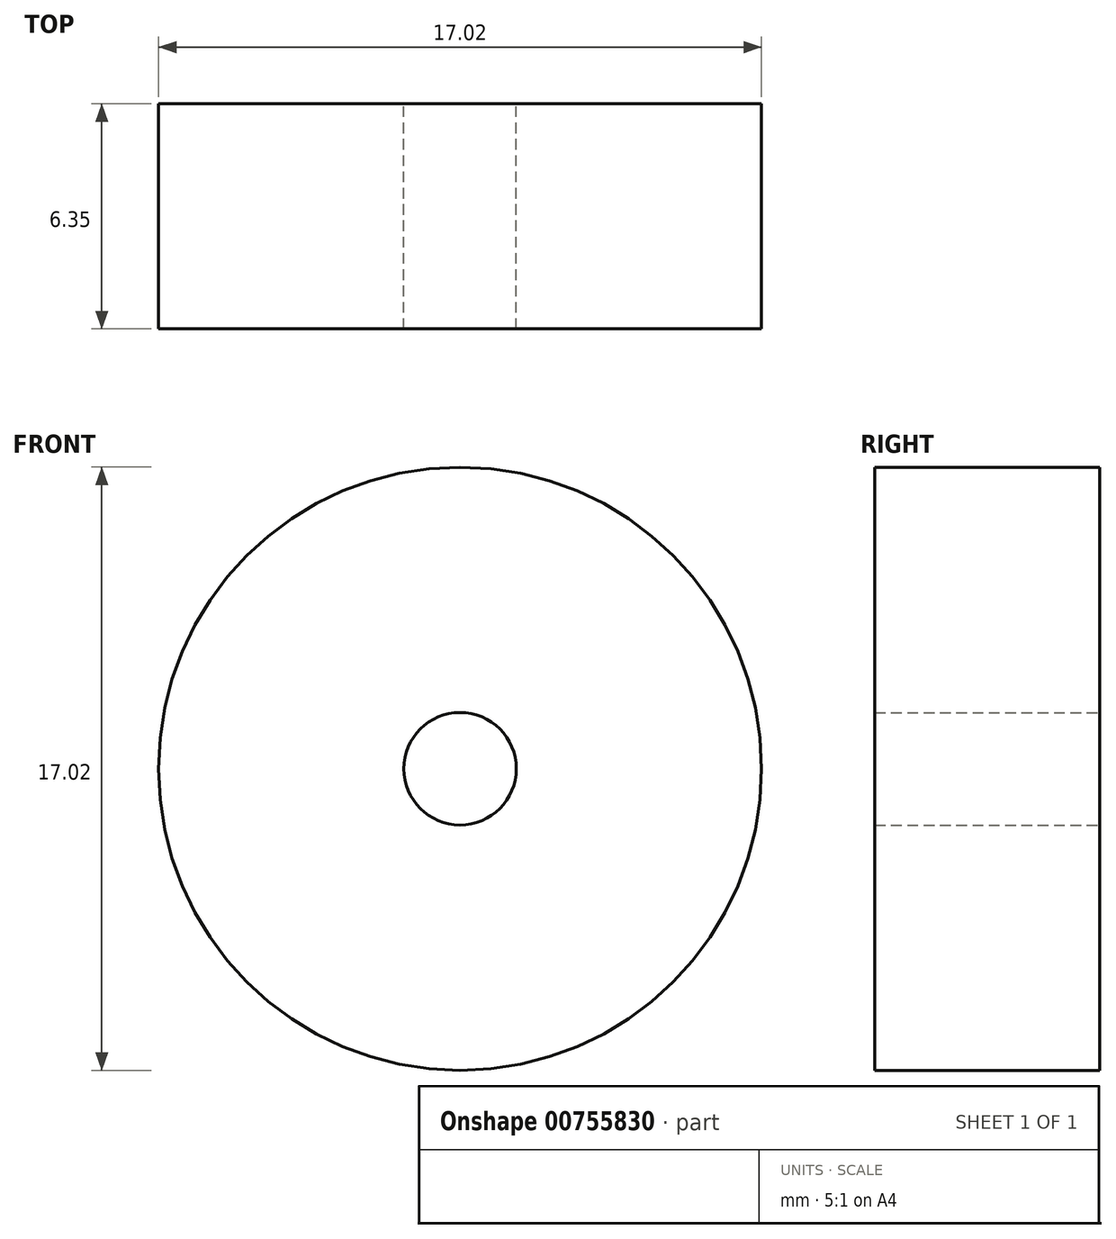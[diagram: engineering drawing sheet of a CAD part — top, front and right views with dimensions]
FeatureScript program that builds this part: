
annotation { "Feature Type Name" : "Feature", "Feature Type Description" : "" }
export const myFeature = defineFeature(function(context is Context, id is Id, definition is map)
    precondition{}
    {
        {
            var Q0;
            Q0=qCreatedBy(makeId("Front.planeOp"),FACE);
            var sketch = newSketch(context, id + "F0", { "sketchPlane" : qUnion([Q0])});
            skCircle(sketch, "E0", {"center": v(0, 0) * mm, "radius": 8.5 * mm});
            skCircle(sketch, "E1", {"center": v(0, 0) * mm, "radius": 1.59 * mm});
            skSolve(sketch);
        }
        {
            var Q0;
            Q0=qSketchRegion(id+"F0",true);
            extrude(context, id + "F1", {"entities" : qUnion([Q0]), "depth" : 6.35 * mm, "offsetDistance" : 25.4 * mm});
        }
    });
